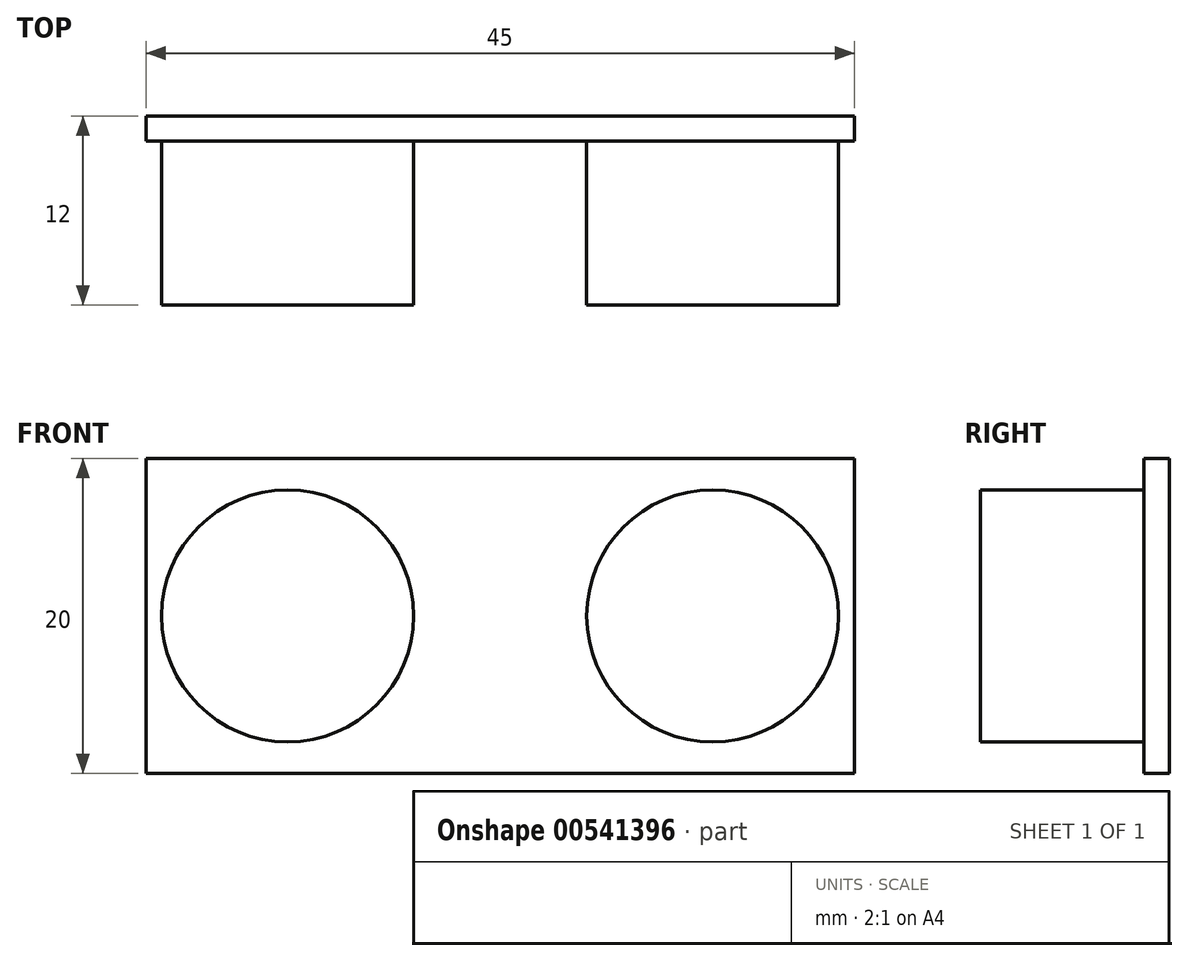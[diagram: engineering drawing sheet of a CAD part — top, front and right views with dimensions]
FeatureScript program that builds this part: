
annotation { "Feature Type Name" : "Feature", "Feature Type Description" : "" }
export const myFeature = defineFeature(function(context is Context, id is Id, definition is map)
    precondition{}
    {
        {
            var Q0;
            Q0=qCreatedBy(makeId("Front.planeOp"),FACE);
            var sketch = newSketch(context, id + "F0", { "sketchPlane" : qUnion([Q0])});
            skLineSegment(sketch, "E0.bottom", {"start": v(22.5, 10) * mm, "end": v(-22.5, 10) * mm});
            skLineSegment(sketch, "E0.top", {"start": v(22.5, -10) * mm, "end": v(-22.5, -10) * mm});
            skLineSegment(sketch, "E0.left", {"start": v(22.5, 10) * mm, "end": v(22.5, -10) * mm});
            skLineSegment(sketch, "E0.right", {"start": v(-22.5, 10) * mm, "end": v(-22.5, -10) * mm});
            skPoint(sketch, "E0.middle", {"position": v(0, 0) * mm});
            skSolve(sketch);
        }
        {
            var Q0;
            Q0 = qSketchRegion(id + "F0", true);
            extrude(context, id + "F1", {"entities" : qUnion([Q0]), "depth" : 1.6 * mm, "offsetDistance" : 25 * mm});
        }
        {
            var Q0;
            Q0=qCreatedBy(makeId("Front.planeOp"),FACE);
            var sketch = newSketch(context, id + "F2", { "sketchPlane" : qUnion([Q0])});
            skCircle(sketch, "E1", {"center": v(-13.5, 0) * mm, "radius": 8 * mm});
            skCircle(sketch, "E2", {"center": v(13.5, 0) * mm, "radius": 8 * mm});
            skLineSegment(sketch, "E3", {"start": v(0, 10.2) * mm, "end": v(0, -10.2) * mm});
            skLineSegment(sketch, "E4", {"start": v(-13.5, 0) * mm, "end": v(13.5, 0) * mm});
            skPoint(sketch, "E5", {"position": v(0, 0) * mm});
            skSolve(sketch);
        }
        {
            var Q0;
            Q0 = qSketchRegion(id + "F2", true);
            extrude(context, id + "F3", {"entities" : qUnion([Q0]), "operationType" : NewBodyOperationType.ADD, "depth" : 12 * mm, "offsetDistance" : 25 * mm});
        }
    });
